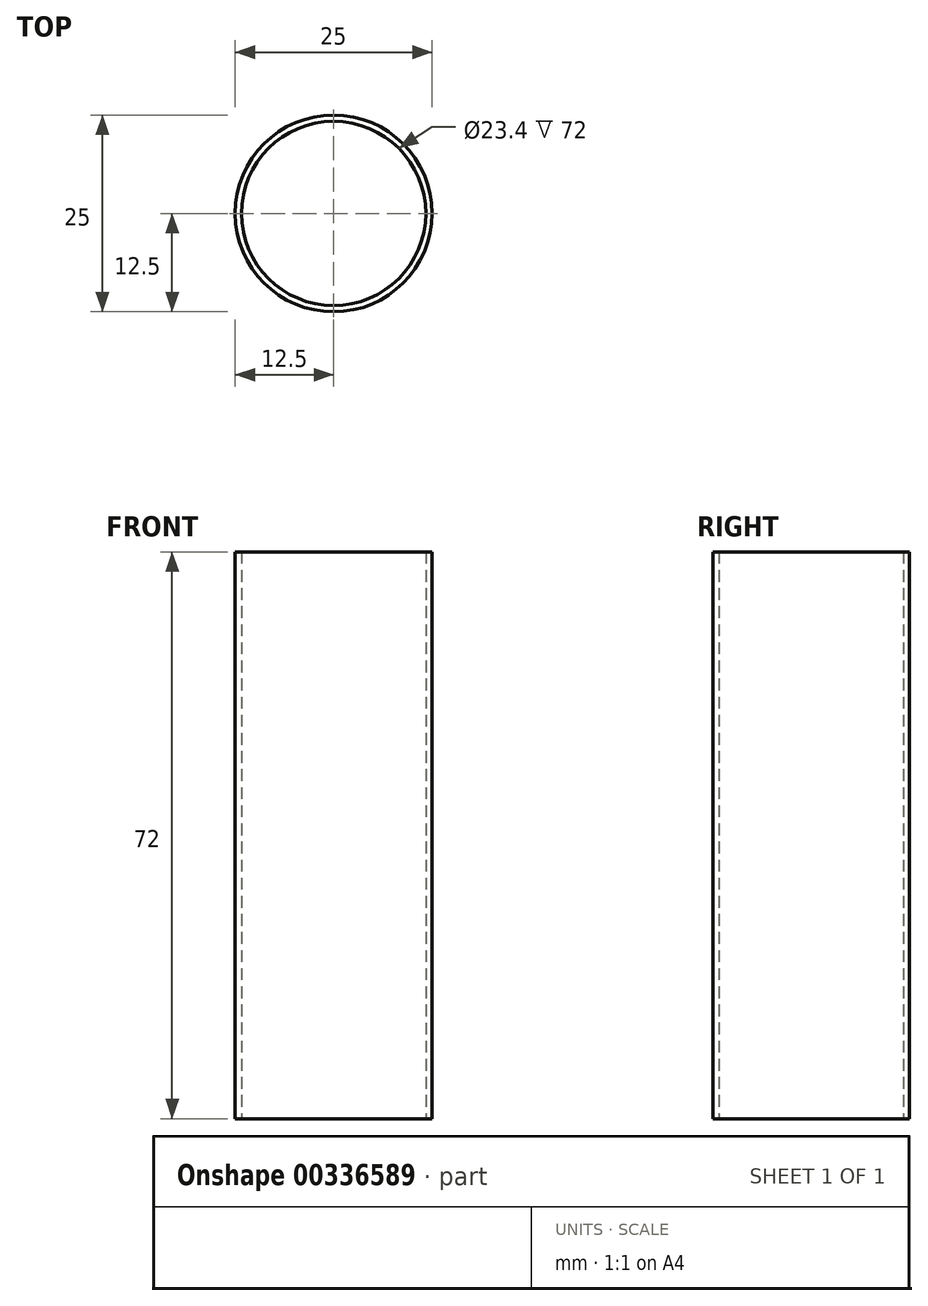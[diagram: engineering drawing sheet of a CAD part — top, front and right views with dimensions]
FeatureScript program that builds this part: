
annotation { "Feature Type Name" : "Feature", "Feature Type Description" : "" }
export const myFeature = defineFeature(function(context is Context, id is Id, definition is map)
    precondition{}
    {
        {
            var Q0;
            Q0=qCreatedBy(makeId("Top.planeOp"),FACE);
            var sketch = newSketch(context, id + "F0", { "sketchPlane" : qUnion([Q0])});
            skCircle(sketch, "E0", {"center": v(0, 0) * mm, "radius": 12.5 * mm});
            skCircle(sketch, "E1.0", {"center": v(0, 0) * mm, "radius": 11.7 * mm});
            skSolve(sketch);
        }
        {
            var Q0;
            Q0=makeQuery(id+"F0.imprint","IMPRINT",FACE,{"disambiguationData":[TD([[makeQuery(id+"F0.imprint","IMPRINT",EDGE,{"derivedFrom":sQuery(id+"F0.wireOp",EDGE,"E0")}),1.0]])]});
            extrude(context, id + "F1", {"entities" : qUnion([Q0]), "depth" : 72 * mm});
        }
    });
